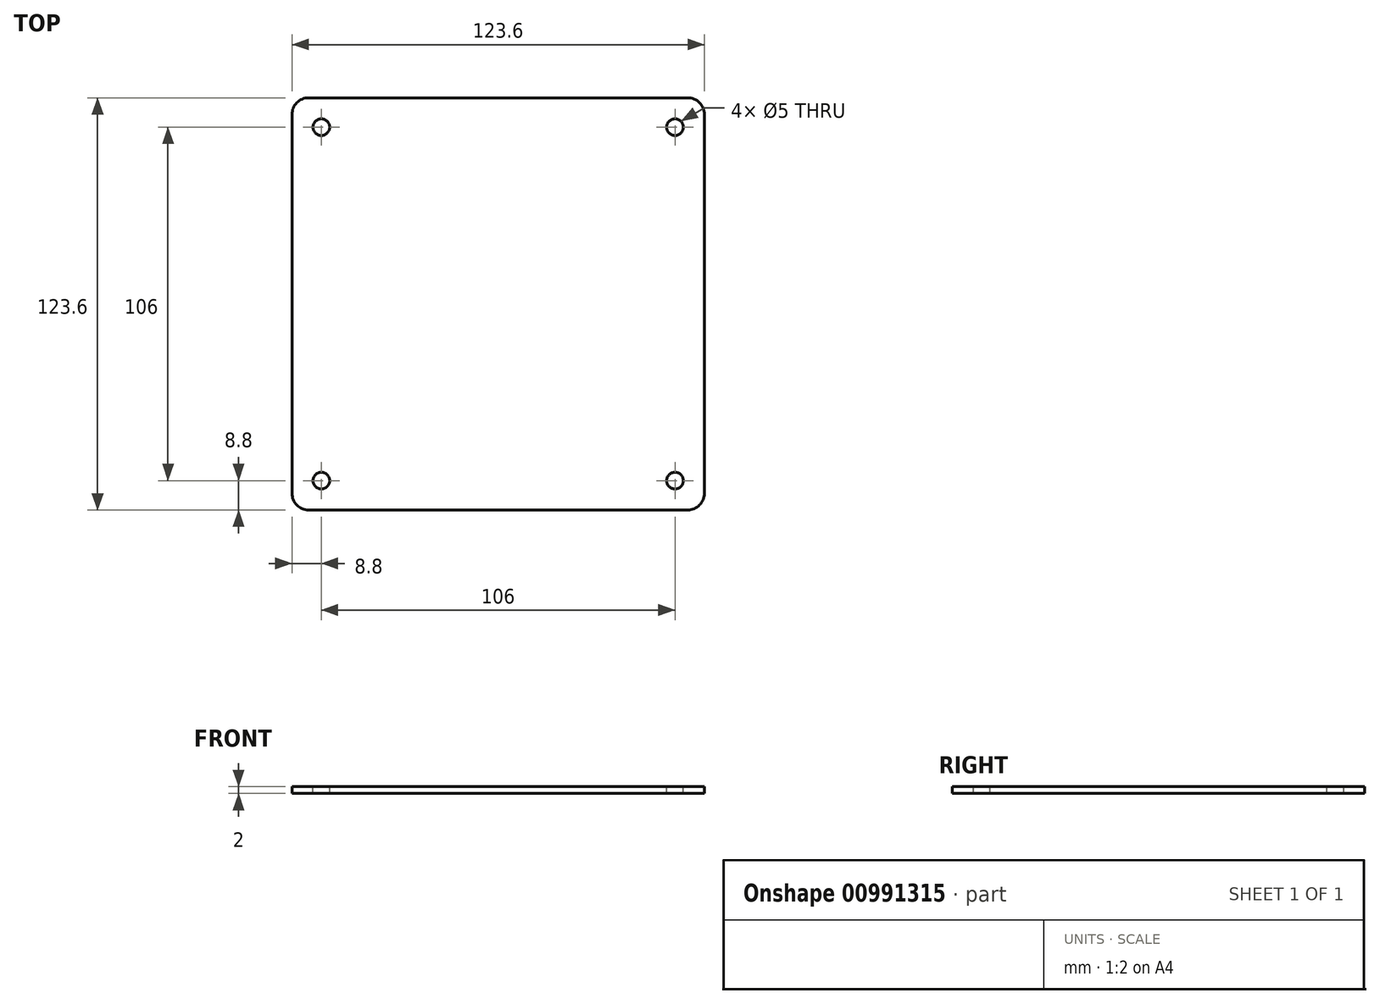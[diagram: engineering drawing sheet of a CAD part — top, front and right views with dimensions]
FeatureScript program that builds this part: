
annotation { "Feature Type Name" : "Feature", "Feature Type Description" : "" }
export const myFeature = defineFeature(function(context is Context, id is Id, definition is map)
    precondition{}
    {
        {
            var Q0;
            Q0=qCreatedBy(makeId("Top.planeOp"),FACE);
            var sketch = newSketch(context, id + "F0", { "sketchPlane" : qUnion([Q0])});
            skLineSegment(sketch, "E0.bottom", {"start": v(-53, 53) * mm, "end": v(53, 53) * mm, "construction": true});
            skLineSegment(sketch, "E0.top", {"start": v(-53, -53) * mm, "end": v(53, -53) * mm, "construction": true});
            skLineSegment(sketch, "E0.left", {"start": v(-53, 53) * mm, "end": v(-53, -53) * mm, "construction": true});
            skLineSegment(sketch, "E0.right", {"start": v(53, 53) * mm, "end": v(53, -53) * mm, "construction": true});
            skPoint(sketch, "E0.middle", {"position": v(0, 0) * mm});
            skLineSegment(sketch, "E1.bottom", {"start": v(-61.8, 61.8) * mm, "end": v(61.8, 61.8) * mm});
            skLineSegment(sketch, "E1.top", {"start": v(-61.8, -61.8) * mm, "end": v(61.8, -61.8) * mm});
            skLineSegment(sketch, "E1.left", {"start": v(-61.8, 61.8) * mm, "end": v(-61.8, -61.8) * mm});
            skLineSegment(sketch, "E1.right", {"start": v(61.8, 61.8) * mm, "end": v(61.8, -61.8) * mm});
            skSolve(sketch);
        }
        {
            var Q0;
            Q0=makeQuery(id+"F0.imprint","IMPRINT",FACE,{"disambiguationData":[TD([[makeQuery(id+"F0.imprint","IMPRINT",EDGE,{"derivedFrom":sQuery(id+"F0.wireOp",EDGE,"E1.bottom")}),-1.0]])]});
            extrude(context, id + "F1", {"entities" : qUnion([Q0]), "depth" : 2 * mm, "offsetDistance" : 25 * mm});
        }
        {
            var Q0;
            Q0=sQuery(id+"F0.wireOp",VERTEX,"E0.bottom.start");
            var Q1;
            Q1=sQuery(id+"F0.wireOp",VERTEX,"E0.bottom.end");
            var Q2;
            Q2=sQuery(id+"F0.wireOp",VERTEX,"E0.top.start");
            var Q3;
            Q3=sQuery(id+"F0.wireOp",VERTEX,"E0.top.end");
            var Q4;
            Q4=makeQuery(id+"F1.opExtrude","SWEPT_BODY",BODY,{"disambiguationData":[OSD([sQuery(id+"F0.wireOp",EDGE,"E1.bottom"),sQuery(id+"F0.wireOp",EDGE,"E1.top"),sQuery(id+"F0.wireOp",EDGE,"E1.left"),sQuery(id+"F0.wireOp",EDGE,"E1.right")])]});
            hole(context, id + "F2", {"style" : HoleStyle.SIMPLE, "endStyle" : HoleEndStyle.BLIND, "oppositeDirection" : true, "holeDiameter" : 5 * mm, "majorDiameter" : 5 * mm, "holeDepth" : 4 * mm, "isTappedThrough" : true, "tappedDepth" : 12 * mm, "tapClearance" : 3, "locations" : qUnion([Q0, Q1, Q2, Q3]), "scope" : qUnion([Q4]), "startStyle" : HoleStartStyle.PART});
        }
        {
            var Q0;
            Q0=makeQuery(id+"F1.opExtrude","SWEPT_EDGE",EDGE,{"disambiguationData":[OSD([sQuery(id+"F0.wireOp",EDGE,"E1.top"),sQuery(id+"F0.wireOp",EDGE,"E1.right")])]});
            var Q1;
            Q1=makeQuery(id+"F1.opExtrude","SWEPT_EDGE",EDGE,{"disambiguationData":[OSD([sQuery(id+"F0.wireOp",EDGE,"E1.top"),sQuery(id+"F0.wireOp",EDGE,"E1.left")])]});
            var Q2;
            Q2=makeQuery(id+"F1.opExtrude","SWEPT_EDGE",EDGE,{"disambiguationData":[OSD([sQuery(id+"F0.wireOp",EDGE,"E1.bottom"),sQuery(id+"F0.wireOp",EDGE,"E1.left")])]});
            var Q3;
            Q3=makeQuery(id+"F1.opExtrude","SWEPT_EDGE",EDGE,{"disambiguationData":[OSD([sQuery(id+"F0.wireOp",EDGE,"E1.bottom"),sQuery(id+"F0.wireOp",EDGE,"E1.right")])]});
            fillet(context, id + "F3", {"entities" : qUnion([Q0, Q1, Q2, Q3]), "tangentPropagation" : true, "radius" : 5 * mm, "defaultsChanged" : false, "vertexSettings" : [], "allowEdgeOverflow" : false});
        }
    });
